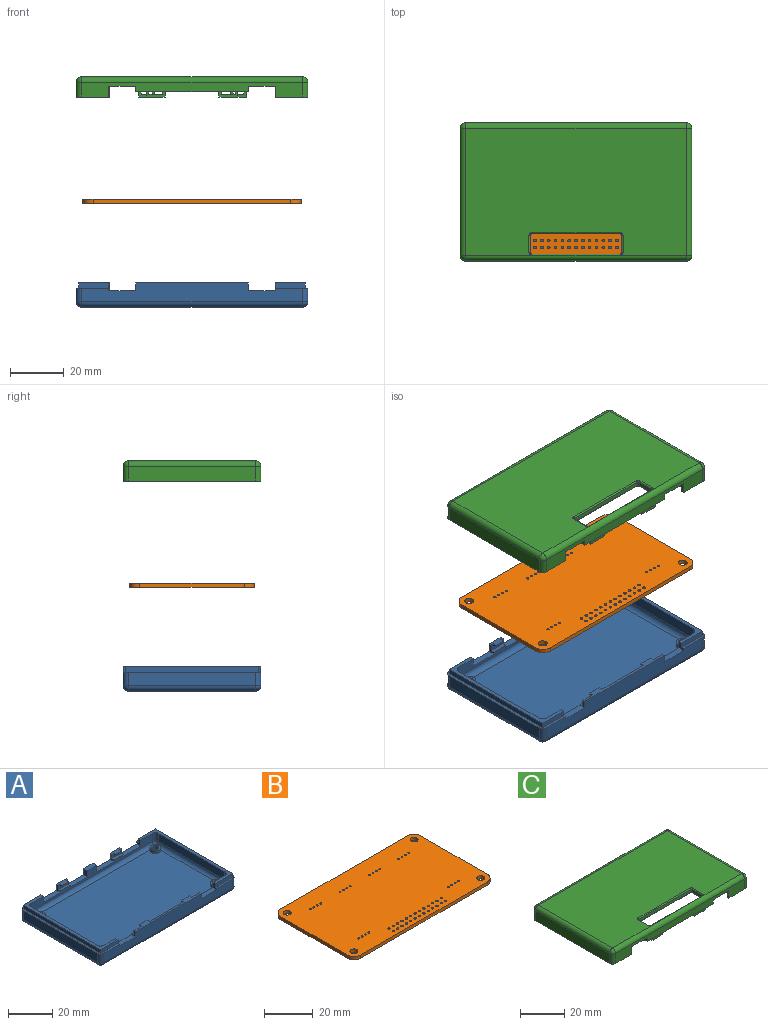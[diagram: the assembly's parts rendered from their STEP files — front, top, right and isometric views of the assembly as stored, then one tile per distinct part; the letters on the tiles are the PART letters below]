
ASSEMBLY  parts=3 mates=3
PART A: 104 faces, bbox 86.3x51.4x9 mm
  f0: plane 77.28x42.36mm, normal (0,0,1), area 3207.7mm2, adj f35,f37,f40,f44,f83,f84,f88,f89
  f1: plane 0.09x0.09mm, normal (0,0,1), area 0mm2, adj f37,f83,f88
  f2: plane 0.09x0.09mm, normal (0,0,1), area 0mm2, adj f44,f83,f84
  f3: plane 0.09x0.09mm, normal (0,0,1), area 0mm2, adj f35,f88,f89
  f4: plane 5.85x2.5mm, normal (0,-1,0), area 10.6mm2, adj f30,f32,f68,f71,f76,f77,f78
  f5: plane 6.15x2.5mm, normal (0,-1,0), area 11.4mm2, adj f24,f26,f69,f70,f72,f73,f74
  f6: plane 82.28x7mm, normal (0,1,0), area 386.1mm2, adj f15,f22,f23,f24,f25,f26,f27,f28
  f7: plane 77.28x4.5mm, normal (0,-1,0), area 168.2mm2, adj f15,f22,f23,f24,f25,f26,f27,f28
  f8: plane 42.07x2.5mm, normal (0,1,0), area 95.2mm2, adj f19,f21,f58,f59,f60,f61,f62,f64
  f9: plane 82.28x7mm, normal (0,-1,0), area 477.5mm2, adj f18,f19,f20,f21,f46,f49,f52,f56
  f10: plane 77.28x4.5mm, normal (0,1,0), area 184.6mm2, adj f18,f19,f20,f21,f46,f51,f52,f57
  f11: plane 47.36x5mm, normal (-1,0,0), area 236.8mm2, adj f49,f92,f96,f97
  f12: plane 47.36x5mm, normal (1,0,0), area 236.8mm2, adj f56,f94,f100,f103
  f13: plane 42.36x4.5mm, normal (1,0,0), area 190.6mm2, adj f51,f85,f89,f91
  f14: plane 42.36x4.5mm, normal (-1,0,0), area 190.6mm2, adj f57,f80,f82,f83
  f15: plane 6.15x2.5mm, normal (0,0,1), area 15.4mm2, adj f6,f7,f27,f29
  f16: plane 82.28x47.36mm, normal (0,0,-1), area 3863.2mm2, adj f34,f38,f41,f43,f95,f96,f100,f101
  f17: plane 0.09x0.09mm, normal (0,0,1), area 0mm2, adj f40,f84,f89
  f18: plane 10x2.5mm, normal (0,0,1), area 25mm2, adj f9,f10,f19,f52
  f19: plane 2.9x2.5mm, normal (1,0,0), area 3.5mm2, adj f8,f9,f10,f18,f58,f59
  f20: plane 10x2.5mm, normal (0,0,1), area 25mm2, adj f9,f10,f21,f46
  f21: plane 2.9x2.5mm, normal (-1,0,0), area 3.5mm2, adj f8,f9,f10,f20,f58,f59
  f22: plane 11x2.5mm, normal (0,0,1), area 27.5mm2, adj f6,f7,f23,f24
  f23: plane 3.4x2.5mm, normal (1,0,0), area 6.5mm2, adj f6,f7,f22,f47,f49,f51
  f24: plane 3.4x2.5mm, normal (-1,0,0), area 4.7mm2, adj f5,f6,f7,f22,f69,f70
  f25: plane 11x2.5mm, normal (0,0,1), area 27.5mm2, adj f6,f7,f26,f27
  f26: plane 3.4x2.5mm, normal (1,0,0), area 4.7mm2, adj f5,f6,f7,f25,f69,f70
  f27: plane 3.4x2.5mm, normal (-1,0,0), area 8.5mm2, adj f6,f7,f15,f25
  f28: plane 11x2.5mm, normal (0,0,1), area 27.5mm2, adj f6,f7,f29,f30
  f29: plane 3.4x2.5mm, normal (1,0,0), area 8.5mm2, adj f6,f7,f15,f28
  f30: plane 3.4x2.5mm, normal (-1,0,0), area 4.7mm2, adj f4,f6,f7,f28,f68,f71
  f31: plane 11x2.5mm, normal (0,0,1), area 27.5mm2, adj f6,f7,f32,f33
  f32: plane 3.4x2.5mm, normal (1,0,0), area 4.7mm2, adj f4,f6,f7,f31,f68,f71
  f33: plane 3.4x2.5mm, normal (-1,0,0), area 6.5mm2, adj f6,f7,f31,f53,f56,f57
  f34: cylinder r=1.62mm len=4mm, axis (0,0,-1), area 40.8mm2, adj f16,f36
  f35: cylinder r=2.5mm len=5mm, axis (0,0,-1), area 23.1mm2, adj f0,f3,f36,f88,f89
  f36: plane 5x5mm, normal (0,0,1), area 11.3mm2, adj f34,f35
  f37: cylinder r=2.5mm len=5mm, axis (0,0,-1), area 23.1mm2, adj f0,f1,f39,f83,f88
  f38: cylinder r=1.62mm len=4mm, axis (0,0,-1), area 40.8mm2, adj f16,f39
  f39: plane 5x5mm, normal (0,0,1), area 11.3mm2, adj f37,f38
  f40: cylinder r=2.5mm len=5mm, axis (0,0,-1), area 23.1mm2, adj f0,f17,f42,f84,f89
  f41: cylinder r=1.62mm len=4mm, axis (0,0,-1), area 40.8mm2, adj f16,f42
  f42: plane 5x5mm, normal (0,0,1), area 11.3mm2, adj f40,f41
  f43: cylinder r=1.62mm len=4mm, axis (0,0,-1), area 40.8mm2, adj f16,f45
  f44: cylinder r=2.5mm len=5mm, axis (0,0,-1), area 23.1mm2, adj f0,f2,f45,f83,f84
  f45: plane 5x5mm, normal (0,0,1), area 11.3mm2, adj f43,f44
  f46: plane 2.9x2.5mm, normal (1,0,0), area 5.2mm2, adj f9,f10,f20,f49,f50,f51
  f47: plane 11.24x2mm, normal (0,1,0), area 22.5mm2, adj f23,f48,f49,f51
  f48: plane 49.36x2mm, normal (-1,0,0), area 98.7mm2, adj f47,f49,f50,f51
  f49: plane 51.36x12.24mm, normal (0,0,1), area 72mm2, adj f6,f9,f11,f23,f46,f47,f48,f50
  f50: plane 11.11x2mm, normal (0,-1,0), area 22.2mm2, adj f46,f48,f49,f51
  f51: plane 49.36x11.24mm, normal (0,0,1), area 104.8mm2, adj f7,f10,f13,f23,f46,f47,f48,f50
  f52: plane 2.9x2.5mm, normal (-1,0,0), area 5.2mm2, adj f9,f10,f18,f55,f56,f57
  f53: plane 10.9x2mm, normal (0,1,0), area 21.8mm2, adj f33,f54,f56,f57
  f54: plane 49.36x2mm, normal (1,0,0), area 98.7mm2, adj f53,f55,f56,f57
  f55: plane 11.11x2mm, normal (0,-1,0), area 22.2mm2, adj f52,f54,f56,f57
  f56: plane 51.36x12.11mm, normal (0,0,1), area 71.6mm2, adj f6,f9,f12,f33,f52,f53,f54,f55
  f57: plane 49.36x11.11mm, normal (0,0,1), area 104.3mm2, adj f7,f10,f14,f33,f52,f53,f54,f55
  f58: plane 42.07x1.5mm, normal (0,0,1), area 63.1mm2, adj f8,f10,f19,f21
  f59: plane 42.07x2.5mm, normal (0,0,1), area 57.1mm2, adj f8,f9,f19,f21,f60,f62,f63,f64
  f60: plane 1.5x1mm, normal (1,0,0), area 1.1mm2, adj f8,f59,f61,f63
  f61: plane 5x1.5mm, normal (0,0.34,-0.94), area 8mm2, adj f8,f60,f62,f63
  f62: plane 1.5x1mm, normal (-1,0,0), area 1.1mm2, adj f8,f59,f61,f63
  f63: plane 5x0.45mm, normal (0,1,0), area 2.3mm2, adj f59,f60,f61,f62
  f64: plane 1.5x1mm, normal (1,0,0), area 1.1mm2, adj f8,f59,f65,f67
  f65: plane 5x1.5mm, normal (0,0.34,-0.94), area 8mm2, adj f8,f64,f66,f67
  f66: plane 1.5x1mm, normal (-1,0,0), area 1.1mm2, adj f8,f59,f65,f67
  f67: plane 5x0.45mm, normal (0,1,0), area 2.3mm2, adj f59,f64,f65,f66
  f68: plane 5.85x1.5mm, normal (0,0,1), area 8.8mm2, adj f4,f7,f30,f32
  f69: plane 6.15x1.5mm, normal (0,0,1), area 9.2mm2, adj f5,f7,f24,f26
  f70: plane 6.15x2.5mm, normal (0,0,1), area 12.1mm2, adj f5,f6,f24,f26,f72,f73,f75
  f71: plane 5.85x2.5mm, normal (0,0,1), area 11.8mm2, adj f4,f6,f30,f32,f76,f77,f79
  f72: plane 1.5x1mm, normal (1,0,0), area 1.1mm2, adj f5,f70,f74,f75
  f73: plane 1.5x1mm, normal (-1,0,0), area 1.1mm2, adj f5,f70,f74,f75
  f74: plane 4x1.5mm, normal (0,-0.34,-0.94), area 6.4mm2, adj f5,f72,f73,f75
  f75: plane 4x0.45mm, normal (0,-1,0), area 1.8mm2, adj f70,f72,f73,f74
  f76: plane 1.5x1mm, normal (1,0,0), area 1.1mm2, adj f4,f71,f78,f79
  f77: plane 1.5x1mm, normal (-1,0,0), area 1.1mm2, adj f4,f71,f78,f79
  f78: plane 4x1.5mm, normal (0,-0.34,-0.94), area 6.4mm2, adj f4,f76,f77,f79
  f79: plane 4x0.45mm, normal (0,-1,0), area 1.8mm2, adj f71,f76,f77,f78
  f80: cylinder r=2mm len=4.5mm, axis (0,0,-1), area 14.1mm2, adj f10,f14,f57,f81
  f81: sphere r=2mm, area 6.3mm2, adj f80,f83,f84
  f82: cylinder r=2mm len=4.5mm, axis (0,0,1), area 14.1mm2, adj f7,f14,f57,f86
  f83: cylinder r=2mm len=42.36mm, axis (0,-1,0), area 129.7mm2, adj f0,f1,f2,f14,f37,f44,f81,f86
  f84: cylinder r=2mm len=77.28mm, axis (-1,0,0), area 239.5mm2, adj f0,f2,f10,f17,f40,f44,f81,f87
  f85: cylinder r=2mm len=4.5mm, axis (0,0,1), area 14.1mm2, adj f10,f13,f51,f87
  f86: sphere r=2mm, area 6.3mm2, adj f82,f83,f88
  f87: sphere r=2mm, area 6.3mm2, adj f84,f85,f89
  f88: cylinder r=2mm len=77.28mm, axis (1,0,0), area 239.5mm2, adj f0,f1,f3,f7,f35,f37,f86,f90
  f89: cylinder r=2mm len=42.36mm, axis (0,1,0), area 129.7mm2, adj f0,f3,f13,f17,f35,f40,f87,f90
  f90: sphere r=2mm, area 6.3mm2, adj f88,f89,f91
  f91: cylinder r=2mm len=4.5mm, axis (0,0,-1), area 14.1mm2, adj f7,f13,f51,f90
  f92: cylinder r=2mm len=5mm, axis (0,0,1), area 15.7mm2, adj f6,f11,f49,f93
  f93: sphere r=2mm, area 6.3mm2, adj f92,f95,f96
  f94: cylinder r=2mm len=5mm, axis (0,0,-1), area 15.7mm2, adj f6,f12,f56,f98
  f95: cylinder r=2mm len=82.28mm, axis (-1,0,0), area 258.5mm2, adj f6,f16,f93,f98
  f96: cylinder r=2mm len=47.36mm, axis (0,-1,0), area 148.8mm2, adj f11,f16,f93,f99
  f97: cylinder r=2mm len=5mm, axis (0,0,-1), area 15.7mm2, adj f9,f11,f49,f99
  f98: sphere r=2mm, area 6.3mm2, adj f94,f95,f100
  f99: sphere r=2mm, area 6.3mm2, adj f96,f97,f101
  f100: cylinder r=2mm len=47.36mm, axis (0,1,0), area 148.8mm2, adj f12,f16,f98,f102
  f101: cylinder r=2mm len=82.28mm, axis (1,0,0), area 258.5mm2, adj f9,f16,f99,f102
  f102: sphere r=2mm, area 6.3mm2, adj f100,f101,f103
  f103: cylinder r=2mm len=5mm, axis (0,0,1), area 15.7mm2, adj f9,f12,f56,f102
PART B: 64 faces, bbox 81.3x46.4x1.6 mm
  f0: plane 73.66x1.6mm, normal (0,1,0), area 117.9mm2, adj f1,f2,f3,f4
  f1: cylinder r=3.81mm len=3.81mm, axis (0,0,-1), area 9.6mm2, adj f0,f3,f4,f5
  f2: cylinder r=3.81mm len=3.81mm, axis (0,0,-1), area 9.6mm2, adj f0,f3,f4,f6
  f3: plane 81.28x46.36mm, normal (0,0,-1), area 3689.7mm2, adj f0,f1,f2,f5,f6,f7,f8,f9
  f4: plane 81.28x46.36mm, normal (0,0,1), area 3689.7mm2, adj f0,f1,f2,f5,f6,f7,f8,f9
  f5: plane 38.74x1.6mm, normal (-1,0,0), area 62mm2, adj f1,f3,f4,f7
  f6: plane 38.74x1.6mm, normal (1,0,0), area 62mm2, adj f2,f3,f4,f8
  f7: cylinder r=3.81mm len=3.81mm, axis (0,0,-1), area 9.6mm2, adj f3,f4,f5,f9
  f8: cylinder r=3.81mm len=3.81mm, axis (0,0,-1), area 9.6mm2, adj f3,f4,f6,f9
  f9: plane 73.66x1.6mm, normal (0,-1,0), area 117.9mm2, adj f3,f4,f7,f8
  f10: cylinder r=0.5mm len=1.6mm, axis (0,0,1), area 5mm2, adj f3,f4
  f11: cylinder r=0.5mm len=1.6mm, axis (0,0,1), area 5mm2, adj f3,f4
  f12: cylinder r=0.5mm len=1.6mm, axis (0,0,1), area 5mm2, adj f3,f4
  f13: cylinder r=0.5mm len=1.6mm, axis (0,0,1), area 5mm2, adj f3,f4
  f14: cylinder r=0.5mm len=1.6mm, axis (0,0,1), area 5mm2, adj f3,f4
  f15: cylinder r=0.5mm len=1.6mm, axis (0,0,1), area 5mm2, adj f3,f4
  f16: cylinder r=0.5mm len=1.6mm, axis (0,0,1), area 5mm2, adj f3,f4
  f17: cylinder r=0.5mm len=1.6mm, axis (0,0,1), area 5mm2, adj f3,f4
  f18: cylinder r=0.5mm len=1.6mm, axis (0,0,1), area 5mm2, adj f3,f4
  f19: cylinder r=0.5mm len=1.6mm, axis (0,0,1), area 5mm2, adj f3,f4
  f20: cylinder r=0.5mm len=1.6mm, axis (0,0,1), area 5mm2, adj f3,f4
  f21: cylinder r=0.5mm len=1.6mm, axis (0,0,1), area 5mm2, adj f3,f4
  f22: cylinder r=0.5mm len=1.6mm, axis (0,0,1), area 5mm2, adj f3,f4
  f23: cylinder r=0.5mm len=1.6mm, axis (0,0,1), area 5mm2, adj f3,f4
  f24: cylinder r=0.5mm len=1.6mm, axis (0,0,1), area 5mm2, adj f3,f4
  f25: cylinder r=0.5mm len=1.6mm, axis (0,0,1), area 5mm2, adj f3,f4
  f26: cylinder r=0.4mm len=1.6mm, axis (0,0,1), area 4mm2, adj f3,f4
  f27: cylinder r=0.4mm len=1.6mm, axis (0,0,1), area 4mm2, adj f3,f4
  f28: cylinder r=0.4mm len=1.6mm, axis (0,0,1), area 4mm2, adj f3,f4
  f29: cylinder r=0.4mm len=1.6mm, axis (0,0,1), area 4mm2, adj f3,f4
  f30: cylinder r=0.4mm len=1.6mm, axis (0,0,1), area 4mm2, adj f3,f4
  f31: cylinder r=0.4mm len=1.6mm, axis (0,0,1), area 4mm2, adj f3,f4
  f32: cylinder r=0.4mm len=1.6mm, axis (0,0,1), area 4mm2, adj f3,f4
  f33: cylinder r=0.4mm len=1.6mm, axis (0,0,1), area 4mm2, adj f3,f4
  f34: cylinder r=0.4mm len=1.6mm, axis (0,0,1), area 4mm2, adj f3,f4
  f35: cylinder r=0.4mm len=1.6mm, axis (0,0,1), area 4mm2, adj f3,f4
  f36: cylinder r=0.4mm len=1.6mm, axis (0,0,1), area 4mm2, adj f3,f4
  f37: cylinder r=0.5mm len=1.6mm, axis (0,0,1), area 5mm2, adj f3,f4
  f38: cylinder r=0.5mm len=1.6mm, axis (0,0,1), area 5mm2, adj f3,f4
  f39: cylinder r=0.5mm len=1.6mm, axis (0,0,1), area 5mm2, adj f3,f4
  f40: cylinder r=0.5mm len=1.6mm, axis (0,0,1), area 5mm2, adj f3,f4
  f41: cylinder r=0.5mm len=1.6mm, axis (0,0,1), area 5mm2, adj f3,f4
  f42: cylinder r=0.5mm len=1.6mm, axis (0,0,1), area 5mm2, adj f3,f4
  f43: cylinder r=0.4mm len=1.6mm, axis (0,0,1), area 4mm2, adj f3,f4
  f44: cylinder r=0.4mm len=1.6mm, axis (0,0,1), area 4mm2, adj f3,f4
  f45: cylinder r=0.4mm len=1.6mm, axis (0,0,1), area 4mm2, adj f3,f4
  f46: cylinder r=0.4mm len=1.6mm, axis (0,0,1), area 4mm2, adj f3,f4
  f47: cylinder r=0.4mm len=1.6mm, axis (0,0,1), area 4mm2, adj f3,f4
  f48: cylinder r=0.4mm len=1.6mm, axis (0,0,1), area 4mm2, adj f3,f4
  f49: cylinder r=0.4mm len=1.6mm, axis (0,0,1), area 4mm2, adj f3,f4
  f50: cylinder r=0.5mm len=1.6mm, axis (0,0,1), area 5mm2, adj f3,f4
  f51: cylinder r=0.4mm len=1.6mm, axis (0,0,1), area 4mm2, adj f3,f4
  f52: cylinder r=0.4mm len=1.6mm, axis (0,0,1), area 4mm2, adj f3,f4
  f53: cylinder r=0.5mm len=1.6mm, axis (0,0,1), area 5mm2, adj f3,f4
  f54: cylinder r=0.5mm len=1.6mm, axis (0,0,1), area 5mm2, adj f3,f4
  f55: cylinder r=0.5mm len=1.6mm, axis (0,0,1), area 5mm2, adj f3,f4
  f56: cylinder r=1.62mm len=3.25mm, axis (0,0,1), area 16.3mm2, adj f3,f4
  f57: cylinder r=1.62mm len=3.25mm, axis (0,0,1), area 16.3mm2, adj f3,f4
  f58: cylinder r=1.62mm len=3.25mm, axis (0,0,1), area 16.3mm2, adj f3,f4
  f59: cylinder r=0.4mm len=1.6mm, axis (0,0,1), area 4mm2, adj f3,f4
  f60: cylinder r=1.62mm len=3.25mm, axis (0,0,1), area 16.3mm2, adj f3,f4
  f61: cylinder r=0.4mm len=1.6mm, axis (0,0,1), area 4mm2, adj f3,f4
  f62: cylinder r=0.4mm len=1.6mm, axis (0,0,1), area 4mm2, adj f3,f4
  f63: cylinder r=0.4mm len=1.6mm, axis (0,0,1), area 4mm2, adj f3,f4
PART C: 127 faces, bbox 86.3x51.4x7.5 mm
  f0: plane 82.28x47.36mm, normal (0,0,1), area 3599.7mm2, adj f97,f98,f102,f103,f108,f109,f113,f114
  f1: plane 7.4x1mm, normal (0,-1,0), area 7.4mm2, adj f11,f38,f81,f83
  f2: plane 5.85x3mm, normal (0,-1,0), area 13.5mm2, adj f8,f35,f37,f69,f70,f71,f72,f83
  f3: plane 6.15x1mm, normal (0,-1,0), area 6.1mm2, adj f12,f32,f34,f83
  f4: plane 6.15x3mm, normal (0,-1,0), area 14.1mm2, adj f9,f29,f31,f62,f63,f64,f65,f66
  f5: plane 42.07x7mm, normal (0,1,0), area 193.5mm2, adj f10,f23,f25,f48,f49,f50,f51,f52
  f6: plane 7.61x1mm, normal (0,1,0), area 7.6mm2, adj f16,f27,f87,f89
  f7: plane 77.28x42.36mm, normal (0,0,-1), area 3063.6mm2, adj f77,f80,f83,f86,f89,f111,f115,f119
  f8: plane 5.85x2.5mm, normal (0,0,-1), area 11.8mm2, adj f2,f13,f35,f37,f69,f71,f73
  f9: plane 6.15x2.5mm, normal (0,0,-1), area 12.4mm2, adj f4,f13,f29,f31,f62,f64,f65,f67
  f10: plane 42.07x2.5mm, normal (0,0,-1), area 99.2mm2, adj f5,f14,f23,f25,f48,f49,f51,f52
  f11: plane 49.36x11.11mm, normal (0,0,-1), area 102.5mm2, adj f1,f15,f19,f24,f38,f44,f45,f46
  f12: plane 6.15x2.5mm, normal (0,0,-1), area 15.4mm2, adj f3,f13,f32,f34
  f13: plane 82.28x5.5mm, normal (0,1,0), area 213.9mm2, adj f8,f9,f12,f28,f29,f30,f31,f32
  f14: plane 82.28x5.5mm, normal (0,-1,0), area 286.4mm2, adj f10,f22,f23,f24,f25,f26,f27,f42
  f15: plane 7.61x1mm, normal (0,1,0), area 7.6mm2, adj f11,f24,f77,f78
  f16: plane 49.36x11.24mm, normal (0,0,-1), area 103mm2, adj f6,f20,f21,f27,f28,f40,f41,f43
  f17: plane 47.36x5.5mm, normal (1,0,0), area 260.5mm2, adj f47,f99,f103,f105
  f18: plane 47.36x5.5mm, normal (-1,0,0), area 260.5mm2, adj f42,f94,f96,f97
  f19: plane 42.36x1mm, normal (-1,0,0), area 42.4mm2, adj f11,f78,f80,f81
  f20: plane 7.74x1mm, normal (0,-1,0), area 7.7mm2, adj f16,f28,f83,f84
  f21: plane 42.36x1mm, normal (1,0,0), area 42.4mm2, adj f16,f84,f86,f87
  f22: plane 10x2.83mm, normal (0,0,-1), area 28.3mm2, adj f14,f23,f24,f77
  f23: plane 2.83x2.1mm, normal (1,0,0), area 5.4mm2, adj f5,f10,f14,f22,f77
  f24: plane 4.1x2.83mm, normal (-1,0,0), area 7.4mm2, adj f11,f14,f15,f22,f46,f47,f77
  f25: plane 2.83x2.1mm, normal (-1,0,0), area 5.4mm2, adj f5,f10,f14,f26,f89
  f26: plane 10x2.83mm, normal (0,0,-1), area 28.3mm2, adj f14,f25,f27,f89
  f27: plane 4.1x2.83mm, normal (1,0,0), area 7.4mm2, adj f6,f14,f16,f26,f42,f43,f89
  f28: plane 4.6x3.3mm, normal (1,0,0), area 8.9mm2, adj f13,f16,f20,f30,f40,f42,f83
  f29: plane 3.3x2.6mm, normal (-1,0,0), area 6.9mm2, adj f4,f9,f13,f30,f83
  f30: plane 11x3.3mm, normal (0,0,-1), area 36.3mm2, adj f13,f28,f29,f83
  f31: plane 3.3x2.6mm, normal (1,0,0), area 6.9mm2, adj f4,f9,f13,f33,f83
  f32: plane 3.3x2.6mm, normal (-1,0,0), area 6.9mm2, adj f3,f12,f13,f33,f83
  f33: plane 11x3.3mm, normal (0,0,-1), area 36.3mm2, adj f13,f31,f32,f83
  f34: plane 3.3x2.6mm, normal (1,0,0), area 6.9mm2, adj f3,f12,f13,f36,f83
  f35: plane 4.6x3.3mm, normal (-1,0,0), area 9.9mm2, adj f2,f8,f13,f36,f72,f73,f83
  f36: plane 11x3.3mm, normal (0,0,-1), area 36.3mm2, adj f13,f34,f35,f83
  f37: plane 4.6x3.3mm, normal (1,0,0), area 9.9mm2, adj f2,f8,f13,f39,f72,f73,f83
  f38: plane 4.6x3.3mm, normal (-1,0,0), area 8.9mm2, adj f1,f11,f13,f39,f44,f47,f83
  f39: plane 11x3.3mm, normal (0,0,-1), area 36.3mm2, adj f13,f37,f38,f83
  f40: plane 9.24x2mm, normal (0,-1,0), area 18.5mm2, adj f16,f28,f42,f92
  f41: plane 45.36x2mm, normal (1,0,0), area 90.7mm2, adj f16,f42,f92,f93
  f42: plane 51.36x12.24mm, normal (0,0,-1), area 73.7mm2, adj f13,f14,f18,f27,f28,f40,f41,f43
  f43: plane 9.11x2mm, normal (0,1,0), area 18.2mm2, adj f16,f27,f42,f93
  f44: plane 8.9x2mm, normal (0,-1,0), area 17.8mm2, adj f11,f38,f47,f90
  f45: plane 45.36x2mm, normal (-1,0,0), area 90.7mm2, adj f11,f47,f90,f91
  f46: plane 9.11x2mm, normal (0,1,0), area 18.2mm2, adj f11,f24,f47,f91
  f47: plane 51.36x12.11mm, normal (0,0,-1), area 73.4mm2, adj f13,f14,f17,f24,f38,f44,f45,f46
  f48: plane 1.5x1mm, normal (-1,0,0), area 1.5mm2, adj f5,f10,f53,f54
  f49: plane 2x1.5mm, normal (1,0,0), area 3mm2, adj f5,f10,f50,f54
  f50: plane 7x1.5mm, normal (0,0,-1), area 10.5mm2, adj f5,f49,f51,f54
  f51: plane 2x1.5mm, normal (-1,0,0), area 3mm2, adj f5,f10,f50,f54
  f52: plane 1.5x1mm, normal (1,0,0), area 1.5mm2, adj f5,f10,f53,f54
  f53: plane 5x1.5mm, normal (0,0,1), area 7.5mm2, adj f5,f48,f52,f54
  f54: plane 7x2mm, normal (0,-1,0), area 9mm2, adj f10,f48,f49,f50,f51,f52,f53
  f55: plane 1.5x1mm, normal (-1,0,0), area 1.5mm2, adj f5,f10,f60,f61
  f56: plane 2x1.5mm, normal (1,0,0), area 3mm2, adj f5,f10,f57,f61
  f57: plane 7x1.5mm, normal (0,0,-1), area 10.5mm2, adj f5,f56,f58,f61
  f58: plane 2x1.5mm, normal (-1,0,0), area 3mm2, adj f5,f10,f57,f61
  f59: plane 1.5x1mm, normal (1,0,0), area 1.5mm2, adj f5,f10,f60,f61
  f60: plane 5x1.5mm, normal (0,0,1), area 7.5mm2, adj f5,f55,f59,f61
  f61: plane 7x2mm, normal (0,-1,0), area 9mm2, adj f10,f55,f56,f57,f58,f59,f60
  f62: plane 1.5x1mm, normal (-1,0,0), area 1.5mm2, adj f4,f9,f63,f68
  f63: plane 4x1.5mm, normal (0,0,1), area 6mm2, adj f4,f62,f64,f68
  f64: plane 1.5x1mm, normal (1,0,0), area 1.5mm2, adj f4,f9,f63,f68
  f65: plane 2x1.5mm, normal (-1,0,0), area 3mm2, adj f4,f9,f66,f68
  f66: plane 6x1.5mm, normal (0,0,-1), area 9mm2, adj f4,f65,f67,f68
  f67: plane 2x1.5mm, normal (1,0,0), area 3mm2, adj f4,f9,f66,f68
  f68: plane 6x2mm, normal (0,1,0), area 8mm2, adj f9,f62,f63,f64,f65,f66,f67
  f69: plane 1.5x1mm, normal (-1,0,0), area 1.5mm2, adj f2,f8,f70,f73
  f70: plane 4x1.5mm, normal (0,0,1), area 6mm2, adj f2,f69,f71,f73
  f71: plane 1.5x1mm, normal (1,0,0), area 1.5mm2, adj f2,f8,f70,f73
  f72: plane 5.85x1.5mm, normal (0,0,-1), area 8.8mm2, adj f2,f35,f37,f73
  f73: plane 5.85x2mm, normal (0,1,0), area 7.7mm2, adj f8,f35,f37,f69,f70,f71,f72
  f74: plane 6.5x2mm, normal (-1,0,0), area 10mm2, adj f117,f120,f123,f124,f126
  f75: plane 33x1.5mm, normal (0,-1,0), area 49.5mm2, adj f112,f113,f119,f120
  f76: plane 6.5x2mm, normal (1,0,0), area 10mm2, adj f107,f109,f110,f111,f112
  f77: cylinder r=2mm len=21.14mm, axis (1,0,0), area 54.8mm2, adj f5,f7,f15,f22,f23,f24,f79,f126
  f78: cylinder r=2mm len=2mm, axis (0,0,-1), area 3.1mm2, adj f11,f15,f19,f79
  f79: sphere r=2mm, area 6.3mm2, adj f77,f78,f80
  f80: cylinder r=2mm len=42.36mm, axis (0,1,0), area 133.1mm2, adj f7,f19,f79,f82
  f81: cylinder r=2mm len=2mm, axis (0,0,1), area 3.1mm2, adj f1,f11,f19,f82
  f82: sphere r=2mm, area 6.3mm2, adj f80,f81,f83
  f83: cylinder r=2mm len=77.28mm, axis (-1,0,0), area 161.2mm2, adj f1,f2,f3,f4,f7,f20,f28,f29
  f84: cylinder r=2mm len=2mm, axis (0,0,-1), area 3.1mm2, adj f16,f20,f21,f85
  f85: sphere r=2mm, area 6.3mm2, adj f83,f84,f86
  f86: cylinder r=2mm len=42.36mm, axis (0,-1,0), area 133.1mm2, adj f7,f21,f85,f88
  f87: cylinder r=2mm len=2mm, axis (0,0,1), area 3.1mm2, adj f6,f16,f21,f88
  f88: sphere r=2mm, area 6.3mm2, adj f86,f87,f89
  f89: cylinder r=2mm len=21.14mm, axis (1,0,0), area 54.8mm2, adj f5,f6,f7,f25,f26,f27,f88,f107
  f90: cylinder r=2mm len=2mm, axis (0,0,1), area 6.3mm2, adj f11,f44,f45,f47
  f91: cylinder r=2mm len=2mm, axis (0,0,1), area 6.3mm2, adj f11,f45,f46,f47
  f92: cylinder r=2mm len=2mm, axis (0,0,-1), area 6.3mm2, adj f16,f40,f41,f42
  f93: cylinder r=2mm len=2mm, axis (0,0,-1), area 6.3mm2, adj f16,f41,f42,f43
  f94: cylinder r=2mm len=5.5mm, axis (0,0,1), area 17.3mm2, adj f13,f18,f42,f95
  f95: sphere r=2mm, area 6.3mm2, adj f94,f97,f98
  f96: cylinder r=2mm len=5.5mm, axis (0,0,-1), area 17.3mm2, adj f14,f18,f42,f100
  f97: cylinder r=2mm len=47.36mm, axis (0,1,0), area 148.8mm2, adj f0,f18,f95,f100
  f98: cylinder r=2mm len=82.28mm, axis (1,0,0), area 258.5mm2, adj f0,f13,f95,f101
  f99: cylinder r=2mm len=5.5mm, axis (0,0,-1), area 17.3mm2, adj f13,f17,f47,f101
  f100: sphere r=2mm, area 6.3mm2, adj f96,f97,f102
  f101: sphere r=2mm, area 6.3mm2, adj f98,f99,f103
  f102: cylinder r=2mm len=82.28mm, axis (-1,0,0), area 258.5mm2, adj f0,f14,f100,f104,f118
  f103: cylinder r=2mm len=47.36mm, axis (0,-1,0), area 148.8mm2, adj f0,f17,f101,f104
  f104: sphere r=2mm, area 6.3mm2, adj f102,f103,f105
  f105: cylinder r=2mm len=5.5mm, axis (0,0,1), area 17.3mm2, adj f14,f17,f47,f104
  f106: bspline ~2.34x1mm, area 0.9mm2, adj f5,f107,f110
  f107: torus R=2.5mm, axis (1,0,0), area 1.7mm2, adj f76,f89,f106,f111
  f108: torus R=1mm, axis (0,0,1), area 0.8mm2, adj f0,f109,f112,f113
  f109: cylinder r=0.5mm len=6.5mm, axis (0,1,0), area 5.1mm2, adj f0,f76,f108,f114
  f110: cylinder r=0.5mm len=2mm, axis (0,0,1), area 1.6mm2, adj f5,f76,f106,f114
  f111: cylinder r=0.5mm len=5mm, axis (0,1,0), area 3.9mm2, adj f7,f76,f107,f115
  f112: cylinder r=0.5mm len=1.5mm, axis (0,0,1), area 1.2mm2, adj f75,f76,f108,f115
  f113: cylinder r=0.5mm len=33mm, axis (1,0,0), area 25.9mm2, adj f0,f75,f108,f116
  f114: torus R=1mm, axis (0,0,1), area 0.8mm2, adj f0,f109,f110,f118
  f115: torus R=1mm, axis (0,0,1), area 0.8mm2, adj f7,f111,f112,f119
  f116: torus R=1mm, axis (0,0,1), area 0.8mm2, adj f0,f113,f117,f120
  f117: cylinder r=0.5mm len=6.5mm, axis (0,-1,0), area 5.1mm2, adj f0,f74,f116,f121
  f118: cylinder r=0.5mm len=33mm, axis (1,0,0), area 25.9mm2, adj f5,f102,f114,f121
  f119: cylinder r=0.5mm len=33mm, axis (1,0,0), area 25.9mm2, adj f7,f75,f115,f122
  f120: cylinder r=0.5mm len=1.5mm, axis (0,0,-1), area 1.2mm2, adj f74,f75,f116,f122
  f121: torus R=1mm, axis (0,0,1), area 0.8mm2, adj f0,f117,f118,f123
  f122: torus R=1mm, axis (0,0,1), area 0.8mm2, adj f7,f119,f120,f124
  f123: cylinder r=0.5mm len=2mm, axis (0,0,-1), area 1.6mm2, adj f5,f74,f121,f125
  f124: cylinder r=0.5mm len=5mm, axis (0,-1,0), area 3.9mm2, adj f7,f74,f122,f126
  f125: bspline ~2.34x1mm, area 0.9mm2, adj f5,f123,f126
  f126: torus R=2.5mm, axis (1,0,0), area 1.7mm2, adj f74,f77,f124,f125
PLACE A t=(-40.64,0,45.7)mm
PLACE B t=(-168.21,95.57,84.3)mm
PLACE C t=(-40.64,0,96.9)mm
MATE planar C.f14 <-> A.f9  axis (0,-1,0) through (-76.73,-25.68,123.9)mm
MATE planar B.f5 <-> A.f13  axis (-1,0,0) through (-81.28,0,85.1)mm
MATE planar C.f18 <-> A.f11  axis (-1,0,0) through (-83.78,0,126.65)mm
